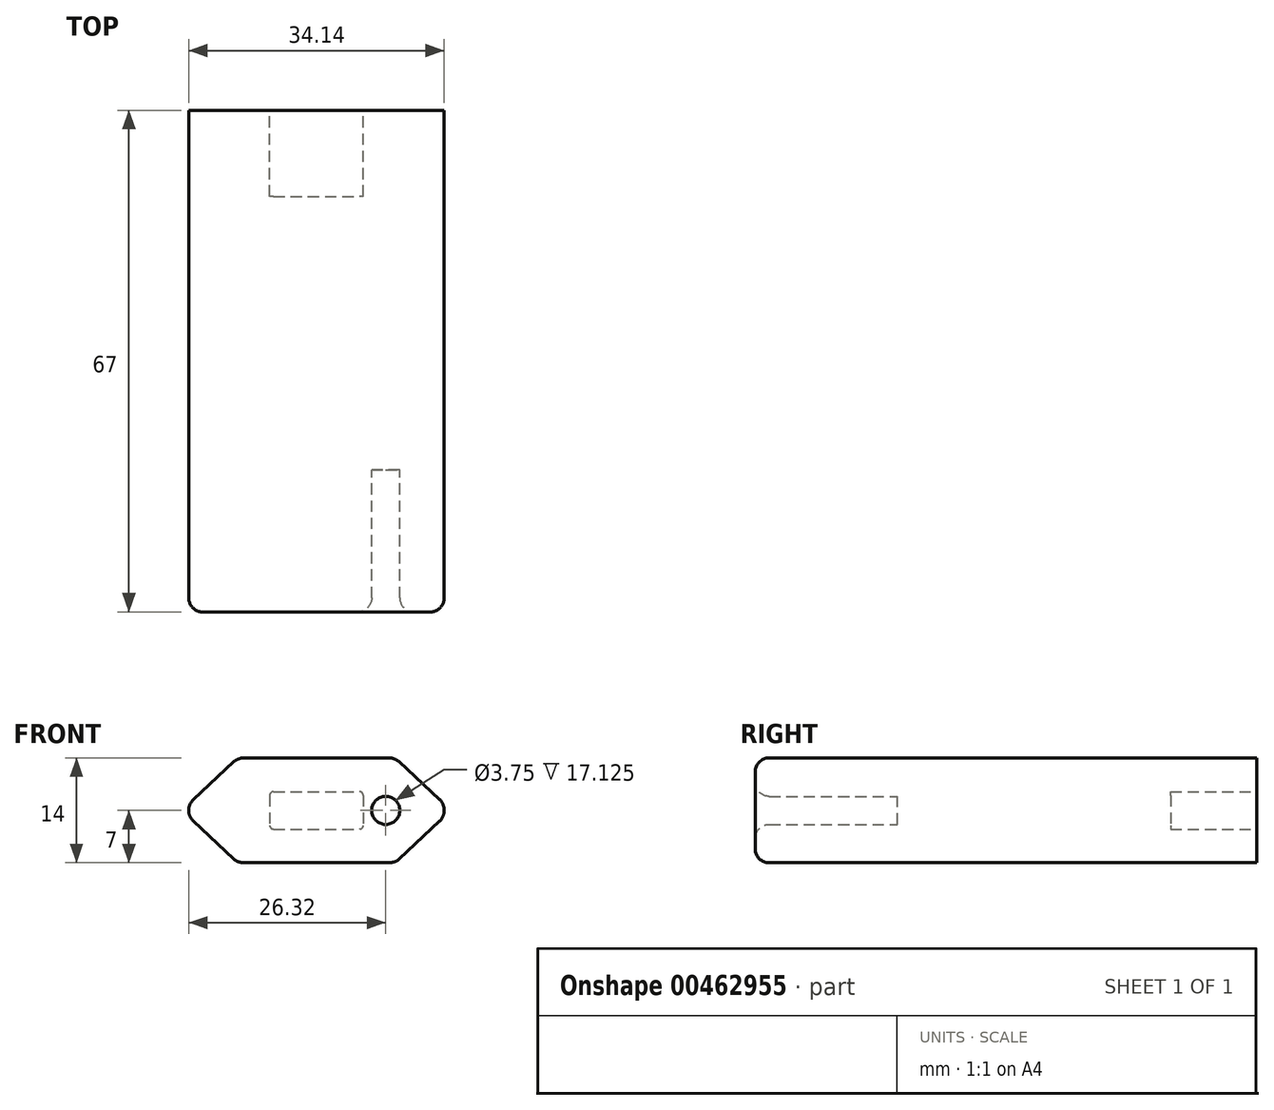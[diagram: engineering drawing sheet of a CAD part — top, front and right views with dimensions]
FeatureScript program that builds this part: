
annotation { "Feature Type Name" : "Feature", "Feature Type Description" : "" }
export const myFeature = defineFeature(function(context is Context, id is Id, definition is map)
    precondition{}
    {
        {
            var Q0;
            Q0=qCreatedBy(makeId("Front.planeOp"),FACE);
            var sketch = newSketch(context, id + "F0", { "sketchPlane" : qUnion([Q0])});
            skLineSegment(sketch, "E0", {"start": v(-16.43, 1.46) * mm, "end": v(-11.08, 6.46) * mm});
            skLineSegment(sketch, "E1", {"start": v(-9.71, 7) * mm, "end": v(9.71, 7) * mm});
            skLineSegment(sketch, "E2", {"start": v(11.08, 6.46) * mm, "end": v(16.43, 1.46) * mm});
            skLineSegment(sketch, "E3", {"start": v(16.43, -1.46) * mm, "end": v(11.08, -6.46) * mm});
            skLineSegment(sketch, "E4", {"start": v(9.71, -7) * mm, "end": v(-9.71, -7) * mm});
            skLineSegment(sketch, "E5", {"start": v(-11.08, -6.46) * mm, "end": v(-16.43, -1.46) * mm});
            skPoint(sketch, "E6.visualSharp", {"position": v(-18, 0) * mm});
            skArc(sketch, "E6.filletArc", {"start": v(-16.43, 1.46) * mm, "mid": v(-17.07, 0) * mm, "end": v(-16.43, -1.46) * mm});
            skPoint(sketch, "E7.visualSharp", {"position": v(-10.5, -7) * mm});
            skArc(sketch, "E7.filletArc", {"start": v(-11.08, -6.46) * mm, "mid": v(-10.45, -6.86) * mm, "end": v(-9.71, -7) * mm});
            skPoint(sketch, "E8.visualSharp", {"position": v(10.5, -7) * mm});
            skArc(sketch, "E8.filletArc", {"start": v(9.71, -7) * mm, "mid": v(10.45, -6.86) * mm, "end": v(11.08, -6.46) * mm});
            skPoint(sketch, "E9.visualSharp", {"position": v(18, 0) * mm});
            skArc(sketch, "E9.filletArc", {"start": v(16.43, -1.46) * mm, "mid": v(17.07, 0) * mm, "end": v(16.43, 1.46) * mm});
            skPoint(sketch, "E10.visualSharp", {"position": v(10.5, 7) * mm});
            skArc(sketch, "E10.filletArc", {"start": v(11.08, 6.46) * mm, "mid": v(10.45, 6.86) * mm, "end": v(9.71, 7) * mm});
            skPoint(sketch, "E11.visualSharp", {"position": v(-10.5, 7) * mm});
            skArc(sketch, "E11.filletArc", {"start": v(-9.71, 7) * mm, "mid": v(-10.45, 6.86) * mm, "end": v(-11.08, 6.46) * mm});
            skSolve(sketch);
        }
        {
            var Q0;
            Q0=makeQuery(id+"F0.imprint","IMPRINT",FACE,{"disambiguationData":[TD([[makeQuery(id+"F0.imprint","IMPRINT",EDGE,{"derivedFrom":sQuery(id+"F0.wireOp",EDGE,"E0")}),-1.0]])]});
            extrude(context, id + "F1", {"entities" : qUnion([Q0]), "endBound" : BoundingType.SYMMETRIC, "depth" : 48 * mm});
        }
        {
            var Q0;
            Q0=makeQuery(id+"F1.opExtrude","CAP_FACE",FACE,{"disambiguationData":[OSD([sQuery(id+"F0.wireOp",EDGE,"E0"),sQuery(id+"F0.wireOp",EDGE,"E1"),sQuery(id+"F0.wireOp",EDGE,"E2"),sQuery(id+"F0.wireOp",EDGE,"E3"),sQuery(id+"F0.wireOp",EDGE,"E4"),sQuery(id+"F0.wireOp",EDGE,"E5"),sQuery(id+"F0.wireOp",EDGE,"E6.filletArc"),sQuery(id+"F0.wireOp",EDGE,"E7.filletArc"),sQuery(id+"F0.wireOp",EDGE,"E8.filletArc"),sQuery(id+"F0.wireOp",EDGE,"E9.filletArc"),sQuery(id+"F0.wireOp",EDGE,"E10.filletArc"),sQuery(id+"F0.wireOp",EDGE,"E11.filletArc")])],"isStart":false});
            var sketch = newSketch(context, id + "F2", { "sketchPlane" : qUnion([Q0])});
            skCircle(sketch, "E12", {"center": v(-9.25, 0) * mm, "radius": 1.88 * mm});
            skCircle(sketch, "E13.MirrorC", {"center": v(9.25, 0) * mm, "radius": 1.88 * mm});
            skSolve(sketch);
        }
        {
            var Q0;
            Q0=makeQuery(id+"F2.imprint","IMPRINT",FACE,{"disambiguationData":[TD([[makeQuery(id+"F2.imprint","IMPRINT",EDGE,{"derivedFrom":sQuery(id+"F2.wireOp",EDGE,"E12")}),1.0]])]});
            var Q1;
            Q1=makeQuery(id+"F2.imprint","IMPRINT",FACE,{"disambiguationData":[TD([[makeQuery(id+"F2.imprint","IMPRINT",EDGE,{"derivedFrom":sQuery(id+"F2.wireOp",EDGE,"E13.MirrorC")}),-1.0]])]});
            extrude(context, id + "F3", {"entities" : qUnion([Q0, Q1]), "operationType" : NewBodyOperationType.ADD, "depth" : 19 * mm});
        }
        {
            var Q0;
            Q0=makeQuery(id+"F3.opExtrude","CAP_FACE",FACE,{"disambiguationData":[OSD([sQuery(id+"F2.wireOp",EDGE,"E12")])],"isStart":false});
            var Q1;
            Q1=makeQuery(id+"F3.opExtrude","CAP_FACE",FACE,{"disambiguationData":[OSD([sQuery(id+"F2.wireOp",EDGE,"E13.MirrorC")])],"isStart":false});
            fillet(context, id + "F4", {"entities" : qUnion([Q0, Q1]), "radius" : 3.75 / 2 * mm, "tangentPropagation" : true, "allowEdgeOverflow" : false});
        }
        {
            var Q0;
            Q0=makeQuery(id+"F1.opExtrude","CAP_FACE",FACE,{"disambiguationData":[OSD([sQuery(id+"F0.wireOp",EDGE,"E0"),sQuery(id+"F0.wireOp",EDGE,"E1"),sQuery(id+"F0.wireOp",EDGE,"E2"),sQuery(id+"F0.wireOp",EDGE,"E3"),sQuery(id+"F0.wireOp",EDGE,"E4"),sQuery(id+"F0.wireOp",EDGE,"E5"),sQuery(id+"F0.wireOp",EDGE,"E6.filletArc"),sQuery(id+"F0.wireOp",EDGE,"E7.filletArc"),sQuery(id+"F0.wireOp",EDGE,"E8.filletArc"),sQuery(id+"F0.wireOp",EDGE,"E9.filletArc"),sQuery(id+"F0.wireOp",EDGE,"E10.filletArc"),sQuery(id+"F0.wireOp",EDGE,"E11.filletArc")])],"isStart":true});
            var sketch = newSketch(context, id + "F5", { "sketchPlane" : qUnion([Q0])});
            skLineSegment(sketch, "E14.bottom", {"start": v(5.75, 2.5) * mm, "end": v(-5.75, 2.5) * mm});
            skLineSegment(sketch, "E14.top", {"start": v(5.75, -2.5) * mm, "end": v(-5.75, -2.5) * mm});
            skLineSegment(sketch, "E14.left", {"start": v(6.25, 2) * mm, "end": v(6.25, -2) * mm});
            skLineSegment(sketch, "E14.right", {"start": v(-6.25, 2) * mm, "end": v(-6.25, -2) * mm});
            skPoint(sketch, "E14.middle", {"position": v(0, 0) * mm});
            skPoint(sketch, "E15.visualSharp", {"position": v(-6.25, 2.5) * mm});
            skArc(sketch, "E15.filletArc", {"start": v(-5.75, 2.5) * mm, "mid": v(-6.1, 2.35) * mm, "end": v(-6.25, 2) * mm});
            skPoint(sketch, "E16.visualSharp", {"position": v(-6.25, -2.5) * mm});
            skArc(sketch, "E16.filletArc", {"start": v(-6.25, -2) * mm, "mid": v(-6.1, -2.35) * mm, "end": v(-5.75, -2.5) * mm});
            skPoint(sketch, "E17.visualSharp", {"position": v(6.25, -2.5) * mm});
            skArc(sketch, "E17.filletArc", {"start": v(5.75, -2.5) * mm, "mid": v(6.1, -2.35) * mm, "end": v(6.25, -2) * mm});
            skPoint(sketch, "E18.visualSharp", {"position": v(6.25, 2.5) * mm});
            skArc(sketch, "E18.filletArc", {"start": v(6.25, 2) * mm, "mid": v(6.1, 2.35) * mm, "end": v(5.75, 2.5) * mm});
            skSolve(sketch);
        }
        {
            var Q0;
            Q0=makeQuery(id+"F5.imprint","IMPRINT",FACE,{"disambiguationData":[TD([[makeQuery(id+"F5.imprint","IMPRINT",EDGE,{"derivedFrom":sQuery(id+"F5.wireOp",EDGE,"E14.bottom")}),1.0]])]});
            extrude(context, id + "F6", {"entities" : qUnion([Q0]), "operationType" : NewBodyOperationType.REMOVE, "oppositeDirection" : true, "depth" : 11.5 * mm});
        }
    });
